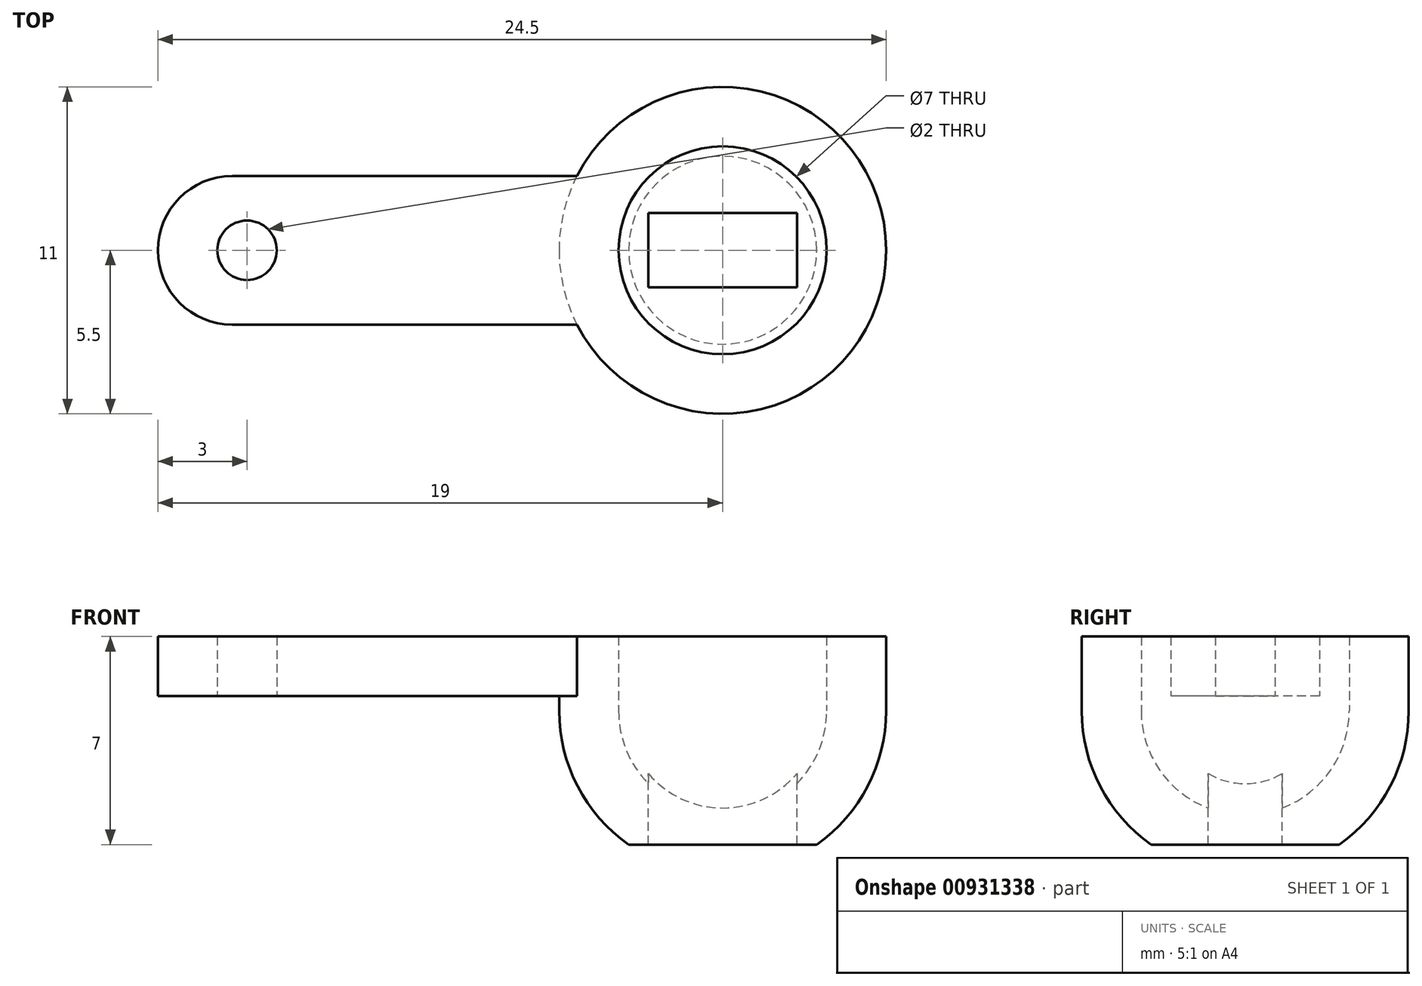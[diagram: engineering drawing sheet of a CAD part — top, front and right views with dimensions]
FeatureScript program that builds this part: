
annotation { "Feature Type Name" : "Feature", "Feature Type Description" : "" }
export const myFeature = defineFeature(function(context is Context, id is Id, definition is map)
    precondition{}
    {
        {
            var Q0;
            Q0=qCreatedBy(makeId("Top.planeOp"),FACE);
            var sketch = newSketch(context, id + "F0", { "sketchPlane" : qUnion([Q0])});
            skLineSegment(sketch, "E0", {"start": v(-7.3, 0) * mm, "end": v(4.56, 0) * mm, "construction": true});
            skLineSegment(sketch, "E1", {"start": v(0, 4.81) * mm, "end": v(0, -4) * mm, "construction": true});
            skLineSegment(sketch, "E2.bottom", {"start": v(-3, 2.5) * mm, "end": v(16, 2.5) * mm});
            skLineSegment(sketch, "E2.top", {"start": v(-3, -2.5) * mm, "end": v(16, -2.5) * mm});
            skLineSegment(sketch, "E2.left", {"start": v(-3, 2.5) * mm, "end": v(-3, -2.5) * mm});
            skLineSegment(sketch, "E2.right", {"start": v(16, 2.5) * mm, "end": v(16, -2.5) * mm});
            skSolve(sketch);
        }
        {
            var Q0;
            Q0=makeQuery(id+"F0.imprint","IMPRINT",FACE,{"disambiguationData":[TD([[makeQuery(id+"F0.imprint","IMPRINT",EDGE,{"derivedFrom":sQuery(id+"F0.wireOp",EDGE,"E2.bottom")}),-1.0]])]});
            extrude(context, id + "F1", {"entities" : qUnion([Q0]), "depth" : 2 * mm, "offsetDistance" : 25 * mm});
        }
        {
            var Q0;
            Q0=qCreatedBy(makeId("Top.planeOp"),FACE);
            cPlane(context, id + "F2", {"entities" : qUnion([Q0]), "cplaneType" : CPlaneType.OFFSET, "offset" : 0.5 * mm, "oppositeDirection" : true, "width" : 150 * mm, "height" : 150 * mm});
        }
        {
            var Q0;
            Q0=qCreatedBy(id+"F2.planeOp",FACE);
            var sketch = newSketch(context, id + "F3", { "sketchPlane" : qUnion([Q0])});
            skLineSegment(sketch, "E3", {"start": v(-26.53, 0) * mm, "end": v(26.6, 0) * mm, "construction": true});
            skLineSegment(sketch, "E4", {"start": v(0, 17.7) * mm, "end": v(0, -28.36) * mm, "construction": true});
            skLineSegment(sketch, "E5", {"start": v(10.5, 0) * mm, "end": v(34.8, 0) * mm});
            skCircle(sketch, "E6", {"center": v(16, 0) * mm, "radius": 5.5 * mm});
            skSolve(sketch);
        }
        {
            var Q0;
            {var subQ0=sQuery(id+"F3.wireOp",EDGE,"E6");var subQ1=sQuery(id+"F3.wireOp",EDGE,"E5");var subQ2=makeQuery(id+"F3.imprint","INTERSECT",VERTEX,{"disambiguationData":[OD(0.0)],"derivedFrom":[subQ1,subQ0]});Q0=makeQuery(id+"F3.imprint","IMPRINT",FACE,{"disambiguationData":[TD([[makeQuery(id+"F3.imprint","IMPRINT",EDGE,{"disambiguationData":[TD([[subQ2,-1.0]])],"derivedFrom":subQ1}),1.0]])]});}
            var Q1;
            Q1=sQuery(id+"F3.wireOp",EDGE,"E5");
            revolve(context, id + "F4", {"operationType" : NewBodyOperationType.ADD, "surfaceOperationType" : NewSurfaceOperationType.NEW, "entities" : qUnion([Q0]), "axis" : qUnion([Q1]), "revolveType" : RevolveType.ONE_DIRECTION, "oppositeDirection" : true, "angle" : 180 * degree});
        }
        {
            var Q0;
            Q0=qCreatedBy(id+"F2.planeOp",FACE);
            var sketch = newSketch(context, id + "F5", { "sketchPlane" : qUnion([Q0])});
            skCircle(sketch, "E7.0", {"center": v(16, 0) * mm, "radius": 5.5 * mm});
            skSolve(sketch);
        }
        {
            var Q0;
            Q0 = qSketchRegion(id + "F5", true);
            var Q1;
            Q1=makeQuery(id+"F1.opExtrude","CAP_FACE",FACE,{"disambiguationData":[OSD([sQuery(id+"F0.wireOp",EDGE,"E2.bottom"),sQuery(id+"F0.wireOp",EDGE,"E2.top"),sQuery(id+"F0.wireOp",EDGE,"E2.left"),sQuery(id+"F0.wireOp",EDGE,"E2.right")])],"isStart":false});
            extrude(context, id + "F6", {"entities" : qUnion([Q0]), "operationType" : NewBodyOperationType.ADD, "endBound" : BoundingType.UP_TO_SURFACE, "depth" : 25 * mm, "endBoundEntityFace" : qUnion([Q1]), "offsetDistance" : 25 * mm});
        }
        {
            var Q0;
            Q0=qCreatedBy(id+"F2.planeOp",FACE);
            var sketch = newSketch(context, id + "F7", { "sketchPlane" : qUnion([Q0])});
            skArc(sketch, "E8.0", {"start": v(11.1, 2.5) * mm, "mid": v(21.5, 0) * mm, "end": v(11.1, -2.5) * mm, "construction": true});
            skCircle(sketch, "E9", {"center": v(16, 0) * mm, "radius": 3.5 * mm});
            skSolve(sketch);
        }
        {
            var Q0;
            Q0 = qSketchRegion(id + "F7", true);
            extrude(context, id + "F8", {"entities" : qUnion([Q0]), "operationType" : NewBodyOperationType.REMOVE, "endBound" : BoundingType.UP_TO_NEXT, "depth" : 25 * mm, "offsetDistance" : 25 * mm});
        }
        {
            var Q0;
            Q0=qCreatedBy(id+"F2.planeOp",FACE);
            var sketch = newSketch(context, id + "F9", { "sketchPlane" : qUnion([Q0])});
            skCircle(sketch, "E10.0", {"center": v(16, 0) * mm, "radius": 3.5 * mm});
            skLineSegment(sketch, "E11", {"start": v(11.73, 0) * mm, "end": v(25.66, 0) * mm});
            skSolve(sketch);
        }
        {
            var Q0;
            {var subQ0=sQuery(id+"F9.wireOp",EDGE,"E11");var subQ1=sQuery(id+"F9.wireOp",EDGE,"E10.0");var subQ2=makeQuery(id+"F9.imprint","INTERSECT",VERTEX,{"disambiguationData":[OD(0.0)],"derivedFrom":[subQ1,subQ0]});Q0=makeQuery(id+"F9.imprint","IMPRINT",FACE,{"disambiguationData":[TD([[makeQuery(id+"F9.imprint","IMPRINT",EDGE,{"disambiguationData":[TD([[subQ2,1.0]])],"derivedFrom":subQ1}),1.0]])]});}
            var Q1;
            Q1=sQuery(id+"F9.wireOp",EDGE,"E11");
            revolve(context, id + "F10", {"operationType" : NewBodyOperationType.REMOVE, "surfaceOperationType" : NewSurfaceOperationType.NEW, "entities" : qUnion([Q0]), "axis" : qUnion([Q1]), "revolveType" : RevolveType.FULL, "oppositeDirection" : true});
        }
        {
            var Q0;
            Q0=qCreatedBy(makeId("Front.planeOp"),FACE);
            var sketch = newSketch(context, id + "F11", { "sketchPlane" : qUnion([Q0])});
            skLineSegment(sketch, "E12.bottom", {"start": v(6, -5) * mm, "end": v(26, -5) * mm});
            skLineSegment(sketch, "E12.top", {"start": v(6, -10) * mm, "end": v(26, -10) * mm});
            skLineSegment(sketch, "E12.left", {"start": v(6, -5) * mm, "end": v(6, -10) * mm});
            skLineSegment(sketch, "E12.right", {"start": v(26, -5) * mm, "end": v(26, -10) * mm});
            skLineSegment(sketch, "E13", {"start": v(-9.12, 0) * mm, "end": v(27.64, 0) * mm, "construction": true});
            skLineSegment(sketch, "E14", {"start": v(0, -8.62) * mm, "end": v(0, 16.95) * mm, "construction": true});
            skLineSegment(sketch, "E15", {"start": v(16, 6.43) * mm, "end": v(16, -18) * mm, "construction": true});
            skSolve(sketch);
        }
        {
            var Q0;
            Q0=makeQuery(id+"F11.imprint","IMPRINT",FACE,{"disambiguationData":[TD([[makeQuery(id+"F11.imprint","IMPRINT",EDGE,{"derivedFrom":sQuery(id+"F11.wireOp",EDGE,"E12.bottom")}),-1.0]])]});
            extrude(context, id + "F12", {"entities" : qUnion([Q0]), "operationType" : NewBodyOperationType.REMOVE, "endBound" : BoundingType.SYMMETRIC, "oppositeDirection" : true, "depth" : 25 * mm, "offsetDistance" : 25 * mm});
        }
        {
            var Q0;
            Q0=qCreatedBy(makeId("Top.planeOp"),FACE);
            var sketch = newSketch(context, id + "F13", { "sketchPlane" : qUnion([Q0])});
            skArc(sketch, "E16.0", {"start": v(11.1, 2.5) * mm, "mid": v(21.5, 0) * mm, "end": v(11.1, -2.5) * mm, "construction": true});
            skLineSegment(sketch, "E17.bottom", {"start": v(13.5, 1.25) * mm, "end": v(18.5, 1.25) * mm});
            skLineSegment(sketch, "E17.top", {"start": v(13.5, -1.25) * mm, "end": v(18.5, -1.25) * mm});
            skLineSegment(sketch, "E17.left", {"start": v(13.5, 1.25) * mm, "end": v(13.5, -1.25) * mm});
            skLineSegment(sketch, "E17.right", {"start": v(18.5, 1.25) * mm, "end": v(18.5, -1.25) * mm});
            skLineSegment(sketch, "E18", {"start": v(-4.95, 0) * mm, "end": v(29.43, 0) * mm, "construction": true});
            skLineSegment(sketch, "E19", {"start": v(16, 6.17) * mm, "end": v(16, -7.71) * mm, "construction": true});
            skSolve(sketch);
        }
        {
            var Q0;
            Q0=makeQuery(id+"F13.imprint","IMPRINT",FACE,{"disambiguationData":[TD([[makeQuery(id+"F13.imprint","IMPRINT",EDGE,{"derivedFrom":sQuery(id+"F13.wireOp",EDGE,"E17.bottom")}),-1.0]])]});
            extrude(context, id + "F14", {"entities" : qUnion([Q0]), "operationType" : NewBodyOperationType.REMOVE, "oppositeDirection" : true, "depth" : 25 * mm, "offsetDistance" : 25 * mm});
        }
        {
            var Q0;
            Q0=qCreatedBy(makeId("Top.planeOp"),FACE);
            var sketch = newSketch(context, id + "F15", { "sketchPlane" : qUnion([Q0])});
            skCircle(sketch, "E20", {"center": v(0, 0) * mm, "radius": 1 * mm});
            skSolve(sketch);
        }
        {
            var Q0;
            Q0 = qSketchRegion(id + "F15", true);
            extrude(context, id + "F16", {"entities" : qUnion([Q0]), "operationType" : NewBodyOperationType.REMOVE, "depth" : 25 * mm, "offsetDistance" : 25 * mm});
        }
        {
            var Q0;
            Q0=makeQuery(id+"F1.opExtrude","SWEPT_EDGE",EDGE,{"disambiguationData":[OSD([sQuery(id+"F0.wireOp",EDGE,"E2.top"),sQuery(id+"F0.wireOp",EDGE,"E2.left")])]});
            var Q1;
            Q1=makeQuery(id+"F1.opExtrude","SWEPT_EDGE",EDGE,{"disambiguationData":[OSD([sQuery(id+"F0.wireOp",EDGE,"E2.bottom"),sQuery(id+"F0.wireOp",EDGE,"E2.left")])]});
            fillet(context, id + "F17", {"entities" : qUnion([Q0, Q1]), "radius" : 2.5 * mm, "tangentPropagation" : true, "allowEdgeOverflow" : false});
        }
    });
